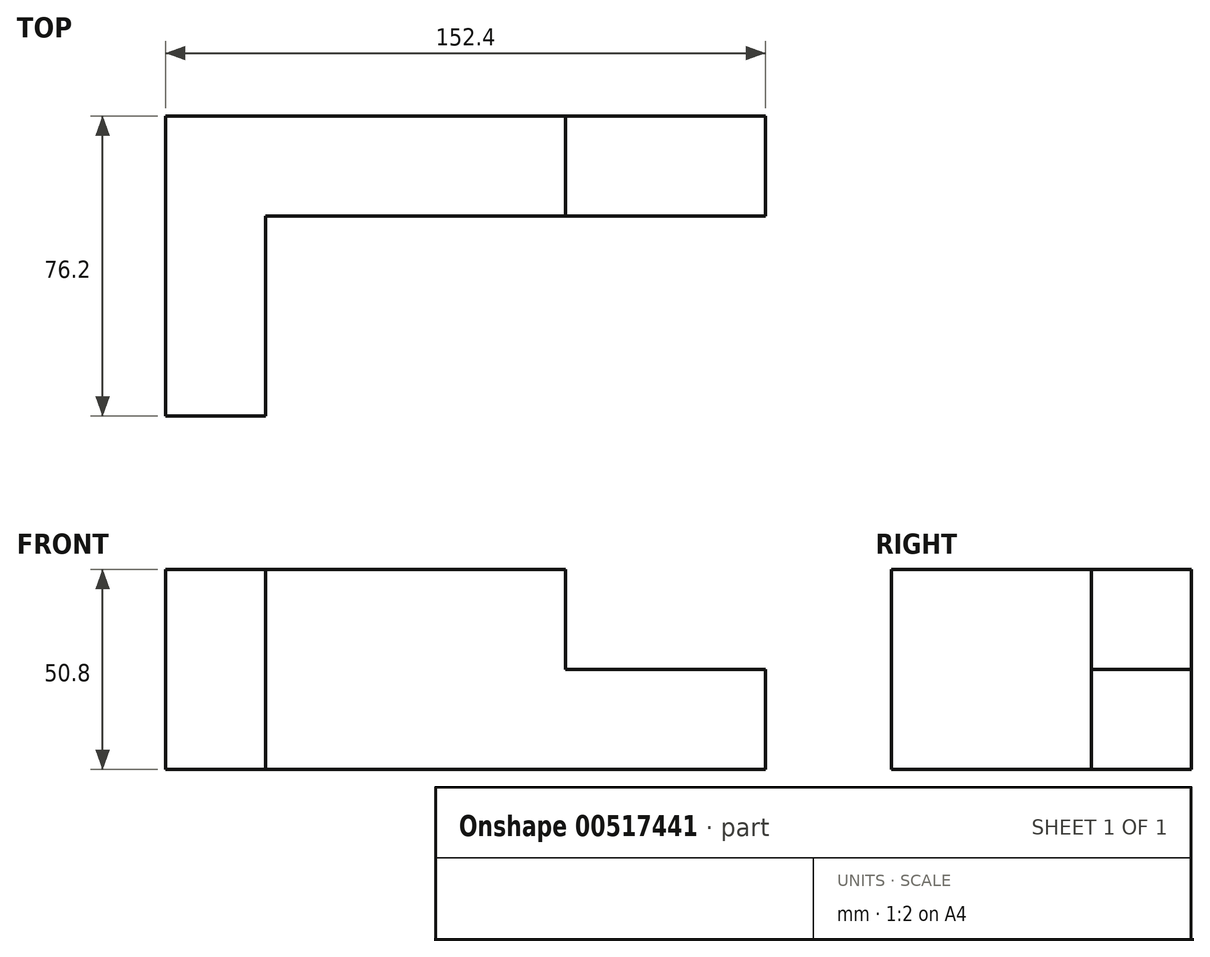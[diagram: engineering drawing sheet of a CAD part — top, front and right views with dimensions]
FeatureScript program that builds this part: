
annotation { "Feature Type Name" : "Feature", "Feature Type Description" : "" }
export const myFeature = defineFeature(function(context is Context, id is Id, definition is map)
    precondition{}
    {
        {
            var Q0;
            Q0=qCreatedBy(makeId("Top.planeOp"),FACE);
            var sketch = newSketch(context, id + "F0", { "sketchPlane" : qUnion([Q0])});
            skLineSegment(sketch, "E0", {"start": v(-115.82, 26) * mm, "end": v(36.58, 26) * mm});
            skLineSegment(sketch, "E1", {"start": v(-115.82, 26) * mm, "end": v(-115.82, -50.2) * mm});
            skLineSegment(sketch, "E2", {"start": v(-115.82, -50.2) * mm, "end": v(-90.42, -50.2) * mm});
            skLineSegment(sketch, "E3", {"start": v(-90.42, -50.2) * mm, "end": v(-90.42, 0.6) * mm});
            skLineSegment(sketch, "E4", {"start": v(-90.42, 0.6) * mm, "end": v(36.58, 0.6) * mm});
            skLineSegment(sketch, "E5", {"start": v(36.58, 26) * mm, "end": v(36.58, 0.6) * mm});
            skLineSegment(sketch, "E6", {"start": v(-115.82, 26) * mm, "end": v(-14.22, 26) * mm});
            skLineSegment(sketch, "E7", {"start": v(-14.22, 26) * mm, "end": v(-14.22, 0.6) * mm});
            skSolve(sketch);
        }
        {
            var Q0;
            Q0=makeQuery(id+"F0.imprint","IMPRINT",FACE,{"disambiguationData":[TD([[makeQuery(id+"F0.imprint","IMPRINT",EDGE,{"derivedFrom":sQuery(id+"F0.wireOp",EDGE,"E1")}),1.0]])]});
            extrude(context, id + "F1", {"entities" : qUnion([Q0]), "depth" : 50.8 * mm, "offsetDistance" : 25.4 * mm});
        }
        {
            var Q0;
            Q0=makeQuery(id+"F0.imprint","IMPRINT",FACE,{"disambiguationData":[TD([[makeQuery(id+"F0.imprint","IMPRINT",EDGE,{"derivedFrom":sQuery(id+"F0.wireOp",EDGE,"E0")}),-1.0]])]});
            extrude(context, id + "F2", {"entities" : qUnion([Q0]), "operationType" : NewBodyOperationType.ADD, "depth" : 25.4 * mm, "offsetDistance" : 25.4 * mm});
        }
    });
